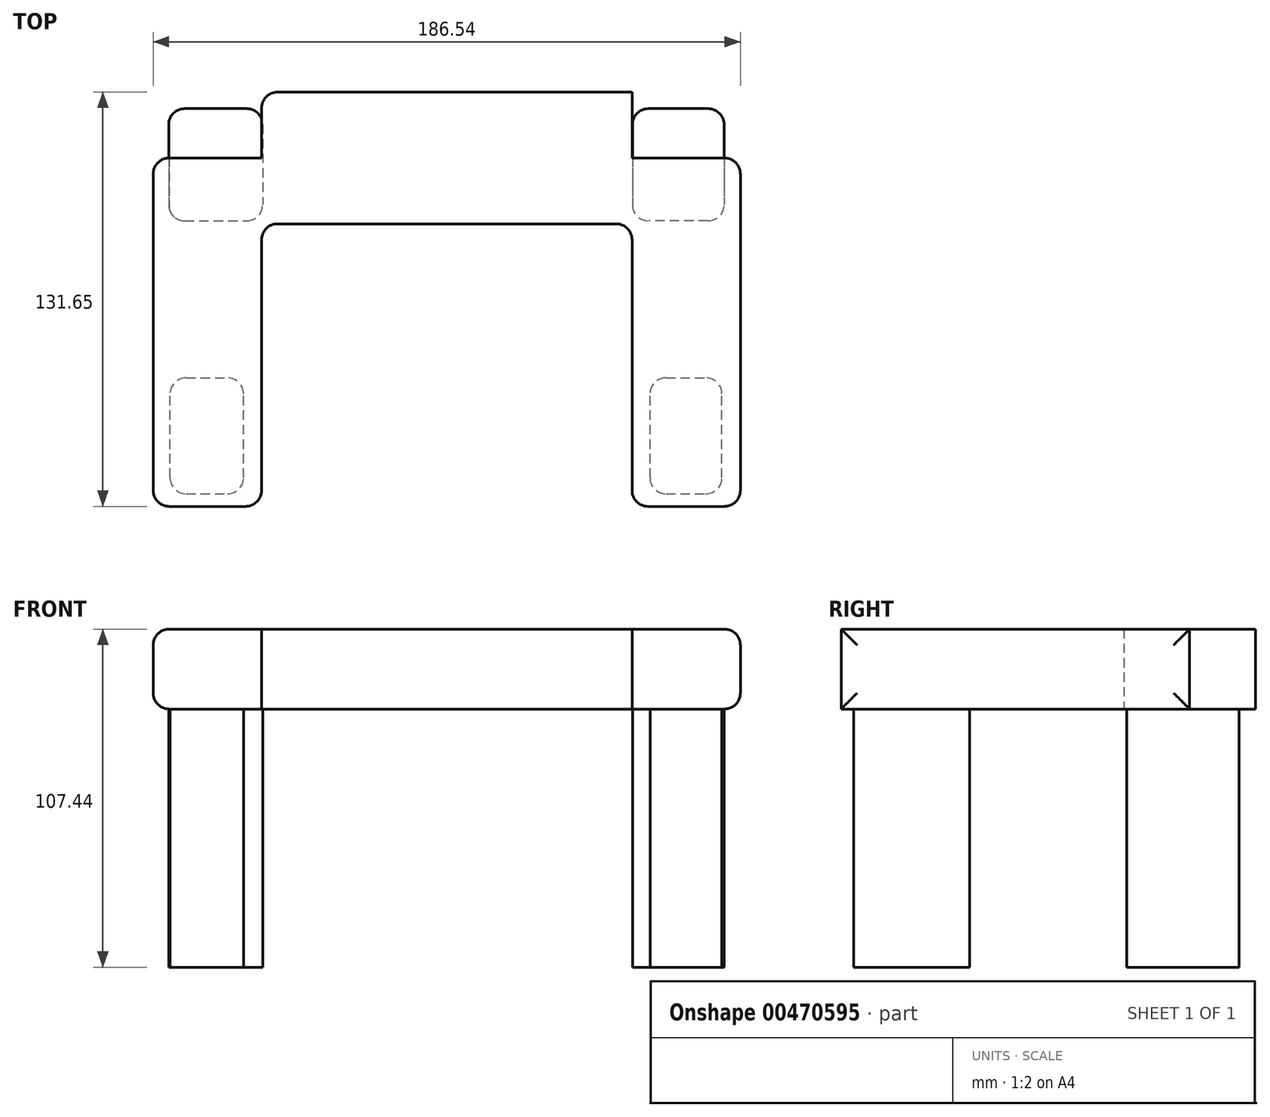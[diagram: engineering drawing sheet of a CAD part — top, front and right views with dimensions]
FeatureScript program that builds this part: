
annotation { "Feature Type Name" : "Feature", "Feature Type Description" : "" }
export const myFeature = defineFeature(function(context is Context, id is Id, definition is map)
    precondition{}
    {
        {
            var Q0;
            Q0=qCreatedBy(makeId("Top.planeOp"),FACE);
            var sketch = newSketch(context, id + "F0", { "sketchPlane" : qUnion([Q0])});
            skLineSegment(sketch, "E0.bottom", {"start": v(-93.27, 55.36) * mm, "end": v(-58.84, 55.36) * mm});
            skLineSegment(sketch, "E0.top", {"start": v(-93.27, -55.36) * mm, "end": v(-58.84, -55.36) * mm});
            skLineSegment(sketch, "E0.left", {"start": v(-93.27, 55.36) * mm, "end": v(-93.27, -55.36) * mm});
            skLineSegment(sketch, "E0.right", {"start": v(-58.84, 55.36) * mm, "end": v(-58.84, -55.36) * mm});
            skPoint(sketch, "E0.middle", {"position": v(-76.06, 0) * mm});
            skLineSegment(sketch, "E1.bottom", {"start": v(-58.84, 76.29) * mm, "end": v(58.84, 76.29) * mm});
            skLineSegment(sketch, "E1.top", {"start": v(-58.84, 34.42) * mm, "end": v(58.84, 34.42) * mm});
            skLineSegment(sketch, "E1.left", {"start": v(-58.84, 76.29) * mm, "end": v(-58.84, 34.42) * mm});
            skLineSegment(sketch, "E1.right", {"start": v(58.84, 76.29) * mm, "end": v(58.84, 34.42) * mm});
            skPoint(sketch, "E1.middle", {"position": v(0, 55.36) * mm});
            skLineSegment(sketch, "E2.bottom", {"start": v(58.84, 55.36) * mm, "end": v(93.27, 55.36) * mm});
            skLineSegment(sketch, "E2.top", {"start": v(58.84, -55.36) * mm, "end": v(93.27, -55.36) * mm});
            skLineSegment(sketch, "E2.left", {"start": v(58.84, 55.36) * mm, "end": v(58.84, -55.36) * mm});
            skLineSegment(sketch, "E2.right", {"start": v(93.27, 55.36) * mm, "end": v(93.27, -55.36) * mm});
            skPoint(sketch, "E2.middle", {"position": v(76.06, 0) * mm});
            skLineSegment(sketch, "E3.bottom", {"start": v(-58.84, 55.36) * mm, "end": v(-93.27, 55.36) * mm});
            skLineSegment(sketch, "E3.top", {"start": v(-58.84, 76.29) * mm, "end": v(-93.27, 76.29) * mm});
            skLineSegment(sketch, "E3.left", {"start": v(-58.84, 55.36) * mm, "end": v(-58.84, 76.29) * mm});
            skLineSegment(sketch, "E3.right", {"start": v(-93.27, 55.36) * mm, "end": v(-93.27, 76.29) * mm});
            skLineSegment(sketch, "E4.top", {"start": v(58.84, 76.52) * mm, "end": v(93.27, 76.52) * mm});
            skLineSegment(sketch, "E4.left", {"start": v(58.84, 55.36) * mm, "end": v(58.84, 76.52) * mm});
            skLineSegment(sketch, "E4.right", {"start": v(93.27, 55.36) * mm, "end": v(93.27, 76.52) * mm});
            skSolve(sketch);
        }
        {
            var Q0;
            Q0=makeQuery(id+"F0.imprint","IMPRINT",FACE,{"disambiguationData":[TD([[makeQuery(id+"F0.imprint","IMPRINT",EDGE,{"derivedFrom":sQuery(id+"F0.wireOp",EDGE,"E3.bottom")}),-1.0]])]});
            var Q1;
            {var subQ3=sQuery(id+"F0.wireOp",EDGE,"E2.bottom");Q1=makeQuery(id+"F0.imprint","IMPRINT",FACE,{"disambiguationData":[TD([[makeQuery(id+"F0.imprint","IMPRINT",EDGE,{"derivedFrom":subQ3}),1.0]])]});}
            var Q2;
            {var subQ4=sQuery(id+"F0.wireOp",EDGE,"E1.bottom");Q2=makeQuery(id+"F0.imprint","IMPRINT",FACE,{"disambiguationData":[TD([[makeQuery(id+"F0.imprint","IMPRINT",EDGE,{"derivedFrom":subQ4}),-1.0]])]});}
            var Q3;
            Q3=makeQuery(id+"F0.imprint","IMPRINT",FACE,{"disambiguationData":[TD([[makeQuery(id+"F0.imprint","IMPRINT",EDGE,{"derivedFrom":sQuery(id+"F0.wireOp",EDGE,"E0.top")}),1.0]])]});
            var Q4;
            {var subQ2=sQuery(id+"F0.wireOp",EDGE,"E2.top");Q4=makeQuery(id+"F0.imprint","IMPRINT",FACE,{"disambiguationData":[TD([[makeQuery(id+"F0.imprint","IMPRINT",EDGE,{"derivedFrom":subQ2}),1.0]])]});}
            extrude(context, id + "F1", {"entities" : qUnion([Q0, Q1, Q2, Q3, Q4]), "depth" : 25.4 * mm});
        }
        {
            var Q0;
            Q0=makeQuery(id+"F1.opExtrude","SWEPT_EDGE",EDGE,{"disambiguationData":[OSD([sQuery(id+"F0.wireOp",EDGE,"E3.top"),sQuery(id+"F0.wireOp",EDGE,"E3.right")])]});
            var Q1;
            Q1=makeQuery(id+"F1.opExtrude","SWEPT_EDGE",EDGE,{"disambiguationData":[OSD([sQuery(id+"F0.wireOp",EDGE,"E4.top"),sQuery(id+"F0.wireOp",EDGE,"E4.right")])]});
            var Q2;
            Q2=makeQuery(id+"F1.opExtrude","SWEPT_FACE",FACE,{"disambiguationData":[OSD([sQuery(id+"F0.wireOp",EDGE,"E2.right"),sQuery(id+"F0.wireOp",EDGE,"E4.right")])]});
            var Q3;
            Q3=makeQuery(id+"F1.opExtrude","SWEPT_FACE",FACE,{"disambiguationData":[OSD([sQuery(id+"F0.wireOp",EDGE,"E4.top")])]});
            var Q4;
            Q4=makeQuery(id+"F1.opExtrude","SWEPT_FACE",FACE,{"disambiguationData":[OSD([sQuery(id+"F0.wireOp",EDGE,"E0.left"),sQuery(id+"F0.wireOp",EDGE,"E3.right")])]});
            var Q5;
            Q5=makeQuery(id+"F1.opExtrude","SWEPT_EDGE",EDGE,{"disambiguationData":[OSD([sQuery(id+"F0.wireOp",EDGE,"E0.right"),sQuery(id+"F0.wireOp",EDGE,"E1.top"),sQuery(id+"F0.wireOp",EDGE,"E1.left")])]});
            var Q6;
            Q6=makeQuery(id+"F1.opExtrude","SWEPT_EDGE",EDGE,{"disambiguationData":[OSD([sQuery(id+"F0.wireOp",EDGE,"E1.top"),sQuery(id+"F0.wireOp",EDGE,"E2.left")])]});
            fillet(context, id + "F2", {"entities" : qUnion([Q0, Q1, Q2, Q3, Q4, Q5, Q6]), "radius" : 5.08 * mm, "tangentPropagation" : true, "allowEdgeOverflow" : false});
        }
        {
            var Q0;
            Q0=makeQuery(id+"F1.opExtrude","SWEPT_EDGE",EDGE,{"disambiguationData":[OSD([sQuery(id+"F0.wireOp",EDGE,"E0.top"),sQuery(id+"F0.wireOp",EDGE,"E0.right")])]});
            var Q1;
            Q1=makeQuery(id+"F1.opExtrude","SWEPT_EDGE",EDGE,{"disambiguationData":[OSD([sQuery(id+"F0.wireOp",EDGE,"E2.top"),sQuery(id+"F0.wireOp",EDGE,"E2.left")])]});
            fillet(context, id + "F3", {"entities" : qUnion([Q0, Q1]), "radius" : 5.08 * mm, "tangentPropagation" : true, "allowEdgeOverflow" : false});
        }
        {
            var Q0;
            Q0=qCreatedBy(makeId("Top.planeOp"),FACE);
            var sketch = newSketch(context, id + "F4", { "sketchPlane" : qUnion([Q0])});
            skLineSegment(sketch, "E5.bottom", {"start": v(-88.34, 71.02) * mm, "end": v(-58.5, 71.02) * mm});
            skLineSegment(sketch, "E5.top", {"start": v(-88.34, 35.36) * mm, "end": v(-58.5, 35.36) * mm});
            skLineSegment(sketch, "E5.left", {"start": v(-88.34, 71.02) * mm, "end": v(-88.34, 35.36) * mm});
            skLineSegment(sketch, "E5.right", {"start": v(-58.5, 71.02) * mm, "end": v(-58.5, 35.36) * mm});
            skLineSegment(sketch, "E6.bottom", {"start": v(88.1, 71.02) * mm, "end": v(58.97, 71.02) * mm});
            skLineSegment(sketch, "E6.top", {"start": v(88.1, 35.36) * mm, "end": v(58.97, 35.36) * mm});
            skLineSegment(sketch, "E6.left", {"start": v(88.1, 71.02) * mm, "end": v(88.1, 35.36) * mm});
            skLineSegment(sketch, "E6.right", {"start": v(58.97, 71.02) * mm, "end": v(58.97, 35.36) * mm});
            skLineSegment(sketch, "E7.bottom", {"start": v(-87.87, -51.35) * mm, "end": v(-64.56, -51.35) * mm});
            skLineSegment(sketch, "E7.top", {"start": v(-87.87, -14.52) * mm, "end": v(-64.56, -14.52) * mm});
            skLineSegment(sketch, "E7.left", {"start": v(-87.87, -51.35) * mm, "end": v(-87.87, -14.52) * mm});
            skLineSegment(sketch, "E7.right", {"start": v(-64.56, -51.35) * mm, "end": v(-64.56, -14.52) * mm});
            skPoint(sketch, "E7.middle", {"position": v(-76.22, -32.94) * mm});
            skLineSegment(sketch, "E8.bottom", {"start": v(64.56, -51.35) * mm, "end": v(87.4, -51.35) * mm});
            skLineSegment(sketch, "E8.top", {"start": v(64.56, -14.52) * mm, "end": v(87.4, -14.52) * mm});
            skLineSegment(sketch, "E8.left", {"start": v(64.56, -51.35) * mm, "end": v(64.56, -14.52) * mm});
            skLineSegment(sketch, "E8.right", {"start": v(87.4, -51.35) * mm, "end": v(87.4, -14.52) * mm});
            skPoint(sketch, "E8.middle", {"position": v(75.98, -32.94) * mm});
            skPoint(sketch, "E8.middle.positionSnap0", {"position": v(-64.56, -32.94) * mm});
            skPoint(sketch, "E8.centerSnap0", {"position": v(-64.56, -32.94) * mm});
            skSolve(sketch);
        }
        {
            var Q0;
            Q0 = qSketchRegion(id + "F4", true);
            extrude(context, id + "F5", {"entities" : qUnion([Q0]), "operationType" : NewBodyOperationType.ADD, "oppositeDirection" : true, "depth" : 82.04 * mm});
        }
        {
            var Q0;
            Q0=makeQuery(id+"F5.opExtrude","SWEPT_EDGE",EDGE,{"disambiguationData":[OSD([sQuery(id+"F4.wireOp",EDGE,"E5.bottom"),sQuery(id+"F4.wireOp",EDGE,"E5.left")])]});
            var Q1;
            Q1=makeQuery(id+"F5.opExtrude","SWEPT_EDGE",EDGE,{"disambiguationData":[OSD([sQuery(id+"F4.wireOp",EDGE,"E6.bottom"),sQuery(id+"F4.wireOp",EDGE,"E6.left")])]});
            var Q2;
            Q2=makeQuery(id+"F5.opExtrude","SWEPT_EDGE",EDGE,{"disambiguationData":[OSD([sQuery(id+"F4.wireOp",EDGE,"E6.bottom"),sQuery(id+"F4.wireOp",EDGE,"E6.right")])]});
            var Q3;
            Q3=makeQuery(id+"F5.opExtrude","SWEPT_EDGE",EDGE,{"disambiguationData":[OSD([sQuery(id+"F4.wireOp",EDGE,"E5.bottom"),sQuery(id+"F4.wireOp",EDGE,"E5.right")])]});
            var Q4;
            Q4=makeQuery(id+"F5.opExtrude","SWEPT_EDGE",EDGE,{"disambiguationData":[OSD([sQuery(id+"F4.wireOp",EDGE,"E5.top"),sQuery(id+"F4.wireOp",EDGE,"E5.right")])]});
            var Q5;
            Q5=makeQuery(id+"F5.opExtrude","SWEPT_EDGE",EDGE,{"disambiguationData":[OSD([sQuery(id+"F4.wireOp",EDGE,"E6.top"),sQuery(id+"F4.wireOp",EDGE,"E6.left")])]});
            var Q6;
            Q6=makeQuery(id+"F5.opExtrude","SWEPT_EDGE",EDGE,{"disambiguationData":[OSD([sQuery(id+"F4.wireOp",EDGE,"E8.top"),sQuery(id+"F4.wireOp",EDGE,"E8.left")])]});
            var Q7;
            Q7=makeQuery(id+"F5.opExtrude","SWEPT_EDGE",EDGE,{"disambiguationData":[OSD([sQuery(id+"F4.wireOp",EDGE,"E8.top"),sQuery(id+"F4.wireOp",EDGE,"E8.right")])]});
            var Q8;
            Q8=makeQuery(id+"F5.opExtrude","SWEPT_EDGE",EDGE,{"disambiguationData":[OSD([sQuery(id+"F4.wireOp",EDGE,"E8.bottom"),sQuery(id+"F4.wireOp",EDGE,"E8.right")])]});
            var Q9;
            Q9=makeQuery(id+"F5.opExtrude","SWEPT_EDGE",EDGE,{"disambiguationData":[OSD([sQuery(id+"F4.wireOp",EDGE,"E8.bottom"),sQuery(id+"F4.wireOp",EDGE,"E8.left")])]});
            var Q10;
            Q10=makeQuery(id+"F5.opExtrude","SWEPT_EDGE",EDGE,{"disambiguationData":[OSD([sQuery(id+"F4.wireOp",EDGE,"E5.top"),sQuery(id+"F4.wireOp",EDGE,"E5.left")])]});
            var Q11;
            Q11=makeQuery(id+"F5.opExtrude","SWEPT_EDGE",EDGE,{"disambiguationData":[OSD([sQuery(id+"F4.wireOp",EDGE,"E6.top"),sQuery(id+"F4.wireOp",EDGE,"E6.right")])]});
            var Q12;
            Q12=makeQuery(id+"F5.opExtrude","SWEPT_EDGE",EDGE,{"disambiguationData":[OSD([sQuery(id+"F4.wireOp",EDGE,"E7.bottom"),sQuery(id+"F4.wireOp",EDGE,"E7.left")])]});
            var Q13;
            Q13=makeQuery(id+"F5.opExtrude","SWEPT_EDGE",EDGE,{"disambiguationData":[OSD([sQuery(id+"F4.wireOp",EDGE,"E7.top"),sQuery(id+"F4.wireOp",EDGE,"E7.left")])]});
            var Q14;
            Q14=makeQuery(id+"F5.opExtrude","SWEPT_EDGE",EDGE,{"disambiguationData":[OSD([sQuery(id+"F4.wireOp",EDGE,"E7.top"),sQuery(id+"F4.wireOp",EDGE,"E7.right")])]});
            var Q15;
            Q15=makeQuery(id+"F5.opExtrude","SWEPT_EDGE",EDGE,{"disambiguationData":[OSD([sQuery(id+"F4.wireOp",EDGE,"E7.bottom"),sQuery(id+"F4.wireOp",EDGE,"E7.right")])]});
            fillet(context, id + "F6", {"entities" : qUnion([Q0, Q1, Q2, Q3, Q4, Q5, Q6, Q7, Q8, Q9, Q10, Q11, Q12, Q13, Q14, Q15]), "radius" : 5.08 * mm, "tangentPropagation" : true, "allowEdgeOverflow" : false});
        }
    });
